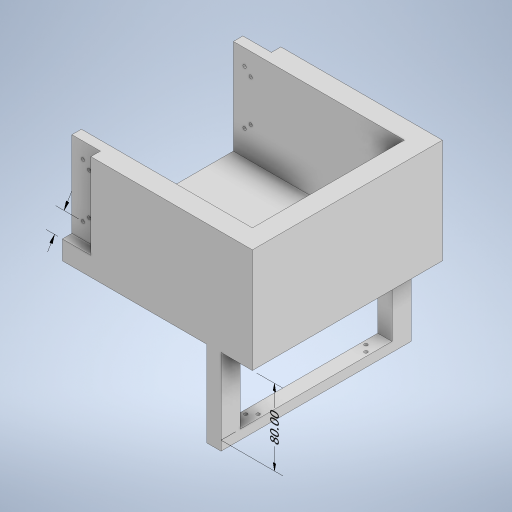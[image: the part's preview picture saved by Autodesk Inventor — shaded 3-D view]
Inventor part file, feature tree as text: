
AUTODESK INVENTOR PART (.ipt)
format: ipt  version: 2023 (Build 270158000, 158)  size: 334,336 bytes
history: native  units: mm
features: sketch x7, extrude x5, other x4, hole x2
ambient origin geometry x8: Origin, YZ Plane, XZ Plane, XY Plane, X Axis, Y Axis, Z Axis, Center Point
bodies: Body1 (feature_tree)
feature tree (18):
  other  "Sólido1"
  other  "Anotaciones"
  extrude  "Extrusión1"  Depth=200.0mm
  hole  "Agujero1"  [1 undecoded]
  extrude  "Extrusión2"  Depth=15.0mm
  extrude  "Extrusión3"  Depth=80.0mm TaperAngle=0.0deg
  extrude  "Extrusión4"  Depth=200.0mm
  extrude  "Extrusión5"  Depth=20.0mm
  hole  "Agujero2"  [1 undecoded]
  sketch  "Boceto2"  dims[d7=15.0mm d8=200.0mm]
  sketch  "Boceto3"  dims[d9=10.0mm d10=0.0mm]
  sketch  "Boceto4"  dims[d12=1.75mm d13=1.75mm d14=1.75mm d15=1.75mm d16=10.0mm d17=10.0mm d19=35.0mm]
  sketch  "Boceto5"  dims[d20=3.5mm d21=6.0mm d22=4.0mm d23=2.0mm d24=90.0deg d25=8.0mm d26=20.594885mm d27=15.0mm]
  sketch  "Boceto6"  dims[d28=20.0mm d29=80.0mm d30=0.0mm]
  sketch  "Boceto7"  dims[d31=48.0mm d32=200.0mm]
  sketch  "Boceto8"  dims[d33=110.0mm d34=0.0mm d36=20.0mm d37=20.0mm d38=20.0mm d39=100.0mm d40=0.0mm d42=10.0mm d43=30.0mm d44=0.0mm d46=1.75mm d47=1.75mm d48=1.75mm d49=1.75mm d50=10.0mm d51=10.0mm d52=15.0mm d56=3.5mm d57=6.0mm d58=4.0mm d59=2.0mm d60=90.0deg d61=8.0mm d62=20.594885mm d63=10.0mm d65=10.0mm d66=10.0mm d67=36.75mm d70=15.0mm d74=200.0mm d78=20.0mm d68=5.348676mm d69=19.508011mm d75=1.454734mm d76=6.982969mm d77=80.0mm]
  other  "Cota lineal 1"
  other  "Cota lineal 2"
note: 2 required parameter values undecoded (feature->parameter linkage not recoverable at this tier; creation-order binding heuristic only, values carry confidence <= 0.55)
